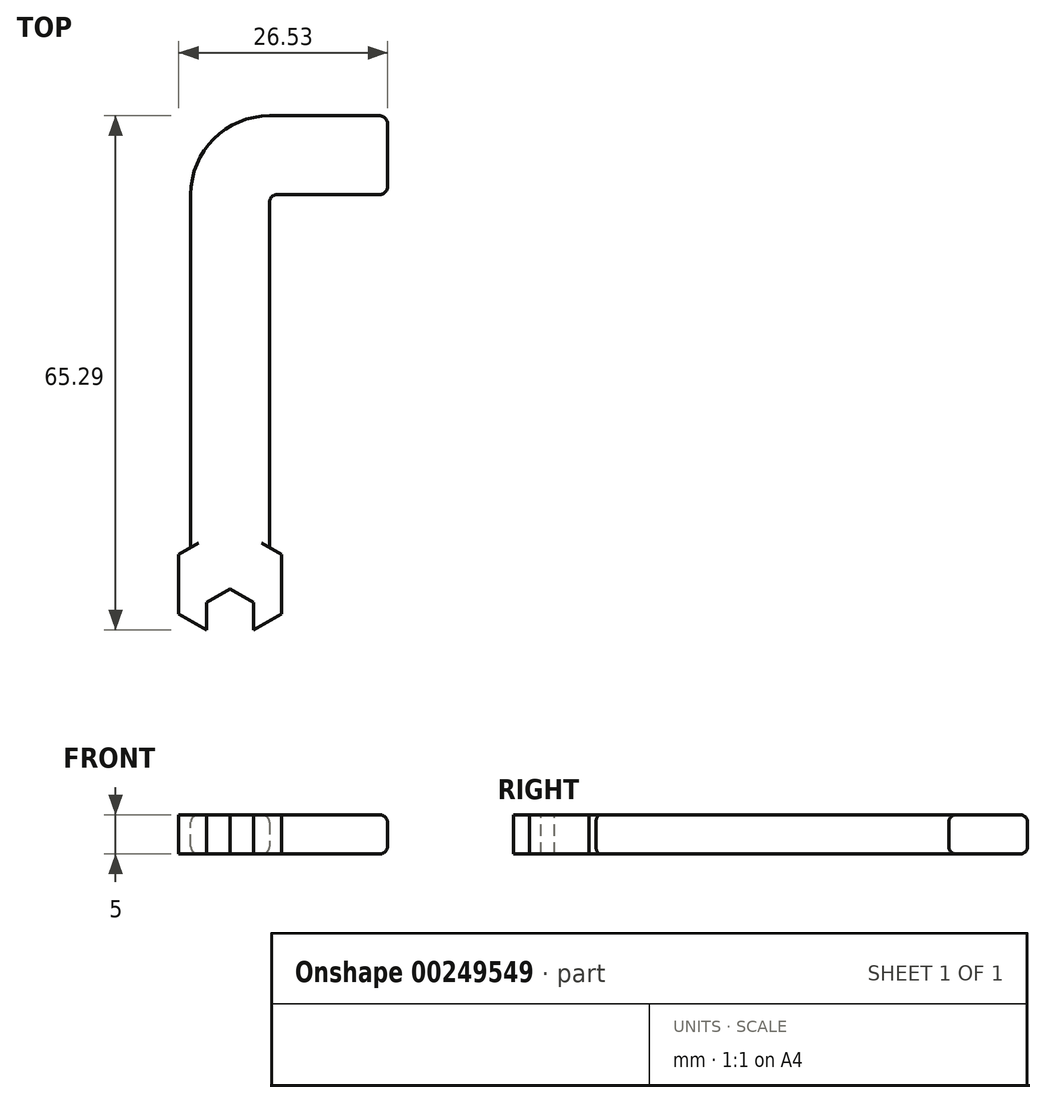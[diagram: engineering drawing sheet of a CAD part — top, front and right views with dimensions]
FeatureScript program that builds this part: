
annotation { "Feature Type Name" : "Feature", "Feature Type Description" : "" }
export const myFeature = defineFeature(function(context is Context, id is Id, definition is map)
    precondition{}
    {
        {
            var Q0;
            Q0=qCreatedBy(makeId("Front.planeOp"),FACE);
            var sketch = newSketch(context, id + "F0", { "sketchPlane" : qUnion([Q0])});
            skLineSegment(sketch, "E0.bottom", {"start": v(5, -2.5) * mm, "end": v(-5, -2.5) * mm});
            skLineSegment(sketch, "E0.top", {"start": v(5, 2.5) * mm, "end": v(-5, 2.5) * mm});
            skLineSegment(sketch, "E0.left", {"start": v(5, -2.5) * mm, "end": v(5, 2.5) * mm});
            skLineSegment(sketch, "E0.right", {"start": v(-5, -2.5) * mm, "end": v(-5, 2.5) * mm});
            skPoint(sketch, "E0.middle", {"position": v(0, 0) * mm});
            skSolve(sketch);
        }
        {
            var Q0;
            Q0=qCreatedBy(makeId("Top.planeOp"),FACE);
            var sketch = newSketch(context, id + "F1", { "sketchPlane" : qUnion([Q0])});
            skLineSegment(sketch, "E1", {"start": v(0, 0) * mm, "end": v(0, 45) * mm});
            skLineSegment(sketch, "E2", {"start": v(5, 50) * mm, "end": v(20, 50) * mm});
            skPoint(sketch, "E3.visualSharp", {"position": v(0, 50) * mm});
            skArc(sketch, "E3.filletArc", {"start": v(5, 50) * mm, "mid": v(1.46, 48.54) * mm, "end": v(0, 45) * mm});
            skSolve(sketch);
        }
        {
            var Q0;
            Q0 = qSketchRegion(id + "F0", true);
            var Q1;
            Q1 = qConstructionFilter(qBodyType(qCreatedBy(id + "F1" ,EDGE), BodyType.WIRE), ConstructionObject.NO);
            sweep(context, id + "F2", {"profiles" : qUnion([Q0]), "path" : qUnion([Q1])});
        }
        {
            var Q0;
            Q0=makeQuery(id+"F2.opSweep","SWEPT_FACE",FACE,{"disambiguationData":[OSD([sQuery(id+"F0.wireOp",EDGE,"E0.top"),sQuery(id+"F1.wireOp",EDGE,"E1")])]});
            var sketch = newSketch(context, id + "F3", { "sketchPlane" : qUnion([Q0])});
            skLineSegment(sketch, "E4.0", {"start": v(-5, 0) * mm, "end": v(5, 0) * mm});
            skLineSegment(sketch, "E4.3", {"start": v(5, -17.32) * mm, "end": v(-5, -17.32) * mm});
            skPoint(sketch, "E4.0.midPoint", {"position": v(0, 0) * mm});
            skCircle(sketch, "E5.cCircle", {"center": v(0, -4.48) * mm, "radius": 6.53 * mm, "construction": true});
            skLineSegment(sketch, "E5.0", {"start": v(6.53, -8.25) * mm, "end": v(0, -12.02) * mm});
            skLineSegment(sketch, "E5.1", {"start": v(0, -12.02) * mm, "end": v(-6.53, -8.25) * mm});
            skLineSegment(sketch, "E5.2", {"start": v(-6.53, -8.25) * mm, "end": v(-6.53, -0.7) * mm});
            skLineSegment(sketch, "E5.3", {"start": v(-6.53, -0.7) * mm, "end": v(0, 3.06) * mm});
            skLineSegment(sketch, "E5.4", {"start": v(0, 3.06) * mm, "end": v(6.53, -0.7) * mm});
            skLineSegment(sketch, "E5.5", {"start": v(6.53, -0.7) * mm, "end": v(6.53, -8.25) * mm});
            skPoint(sketch, "E5.0.midPoint", {"position": v(3.27, -10.14) * mm});
            skSolve(sketch);
        }
        {
            var Q0;
            Q0 = qSketchRegion(id + "F3", true);
            var Q1;
            Q1=makeQuery(id+"F2.opSweep","SWEPT_FACE",FACE,{"disambiguationData":[OSD([sQuery(id+"F0.wireOp",EDGE,"E0.bottom"),sQuery(id+"F1.wireOp",EDGE,"E1")])]});
            extrude(context, id + "F4", {"entities" : qUnion([Q0]), "operationType" : NewBodyOperationType.ADD, "endBound" : BoundingType.UP_TO_SURFACE, "oppositeDirection" : true, "endBoundEntityFace" : qUnion([Q1]), "depth" : 25 * mm});
        }
        {
            var Q0;
            Q0=makeQuery(id+"F4.boolean.opBoolean","MERGE",FACE,{"derivedFrom":[makeQuery(id+"F2.opSweep","SWEPT_FACE",FACE,{"disambiguationData":[OSD([sQuery(id+"F0.wireOp",EDGE,"E0.top"),sQuery(id+"F1.wireOp",EDGE,"E1")])]}),makeQuery(id+"F4.opExtrude","CAP_FACE",FACE,{"disambiguationData":[OSD([sQuery(id+"F3.wireOp",EDGE,"E5.0"),sQuery(id+"F3.wireOp",EDGE,"E5.1"),sQuery(id+"F3.wireOp",EDGE,"E5.2"),sQuery(id+"F3.wireOp",EDGE,"E5.3"),sQuery(id+"F3.wireOp",EDGE,"E5.4"),sQuery(id+"F3.wireOp",EDGE,"E5.5")])],"isStart":true})]});
            var sketch = newSketch(context, id + "F5", { "sketchPlane" : qUnion([Q0])});
            skCircle(sketch, "E6.cCircle", {"center": v(0, -8.56) * mm, "radius": 3 * mm, "construction": true});
            skLineSegment(sketch, "E6.0", {"start": v(3, -10.3) * mm, "end": v(0, -12.02) * mm});
            skLineSegment(sketch, "E6.1", {"start": v(0, -12.02) * mm, "end": v(-3, -10.3) * mm});
            skLineSegment(sketch, "E6.2", {"start": v(-3, -10.3) * mm, "end": v(-3, -6.83) * mm});
            skLineSegment(sketch, "E6.3", {"start": v(-3, -6.83) * mm, "end": v(0, -5.1) * mm});
            skLineSegment(sketch, "E6.4", {"start": v(0, -5.1) * mm, "end": v(3, -6.83) * mm});
            skLineSegment(sketch, "E6.5", {"start": v(3, -6.83) * mm, "end": v(3, -10.3) * mm});
            skPoint(sketch, "E6.0.midPoint", {"position": v(1.5, -11.16) * mm});
            skSolve(sketch);
        }
        {
            var Q0;
            Q0 = qSketchRegion(id + "F5", true);
            extrude(context, id + "F6", {"entities" : qUnion([Q0]), "operationType" : NewBodyOperationType.REMOVE, "endBound" : BoundingType.UP_TO_NEXT, "oppositeDirection" : true, "depth" : 25 * mm});
        }
        {
            var Q0;
            Q0=makeQuery(id+"F2.opSweep","CAP_EDGE",EDGE,{"disambiguationData":[OSD([sQuery(id+"F0.wireOp",EDGE,"E0.right"),sQuery(id+"F1.wireOp",VERTEX,"E2.end")])],"isStart":false});
            var Q1;
            Q1=makeQuery(id+"F2.opSweep","CAP_EDGE",EDGE,{"disambiguationData":[OSD([sQuery(id+"F0.wireOp",EDGE,"E0.left"),sQuery(id+"F1.wireOp",VERTEX,"E2.end")])],"isStart":false});
            var Q2;
            Q2=makeQuery(id+"F2.opSweep","MID_CAP_EDGE",EDGE,{"disambiguationData":[OSD([sQuery(id+"F0.wireOp",EDGE,"E0.left"),sQuery(id+"F1.wireOp",VERTEX,"E3.filletArc.start"),sQuery(id+"F1.wireOp",VERTEX,"E3.filletArc.end")])],"capPos":1.0});
            fillet(context, id + "F7", {"entities" : qUnion([Q0, Q1, Q2]), "radius" : 1 * mm, "tangentPropagation" : true, "allowEdgeOverflow" : false});
        }
        {
            var Q0;
            Q0=makeQuery(id+"F2.opSweep","CAP_EDGE",EDGE,{"disambiguationData":[OSD([sQuery(id+"F0.wireOp",EDGE,"E0.top"),sQuery(id+"F1.wireOp",VERTEX,"E2.end")])],"isStart":false});
            var Q1;
            Q1=makeQuery(id+"F2.opSweep","CAP_EDGE",EDGE,{"disambiguationData":[OSD([sQuery(id+"F0.wireOp",EDGE,"E0.bottom"),sQuery(id+"F1.wireOp",VERTEX,"E2.end")])],"isStart":false});
            fillet(context, id + "F8", {"entities" : qUnion([Q0, Q1]), "radius" : 1 * mm, "tangentPropagation" : true, "allowEdgeOverflow" : false});
        }
    });
